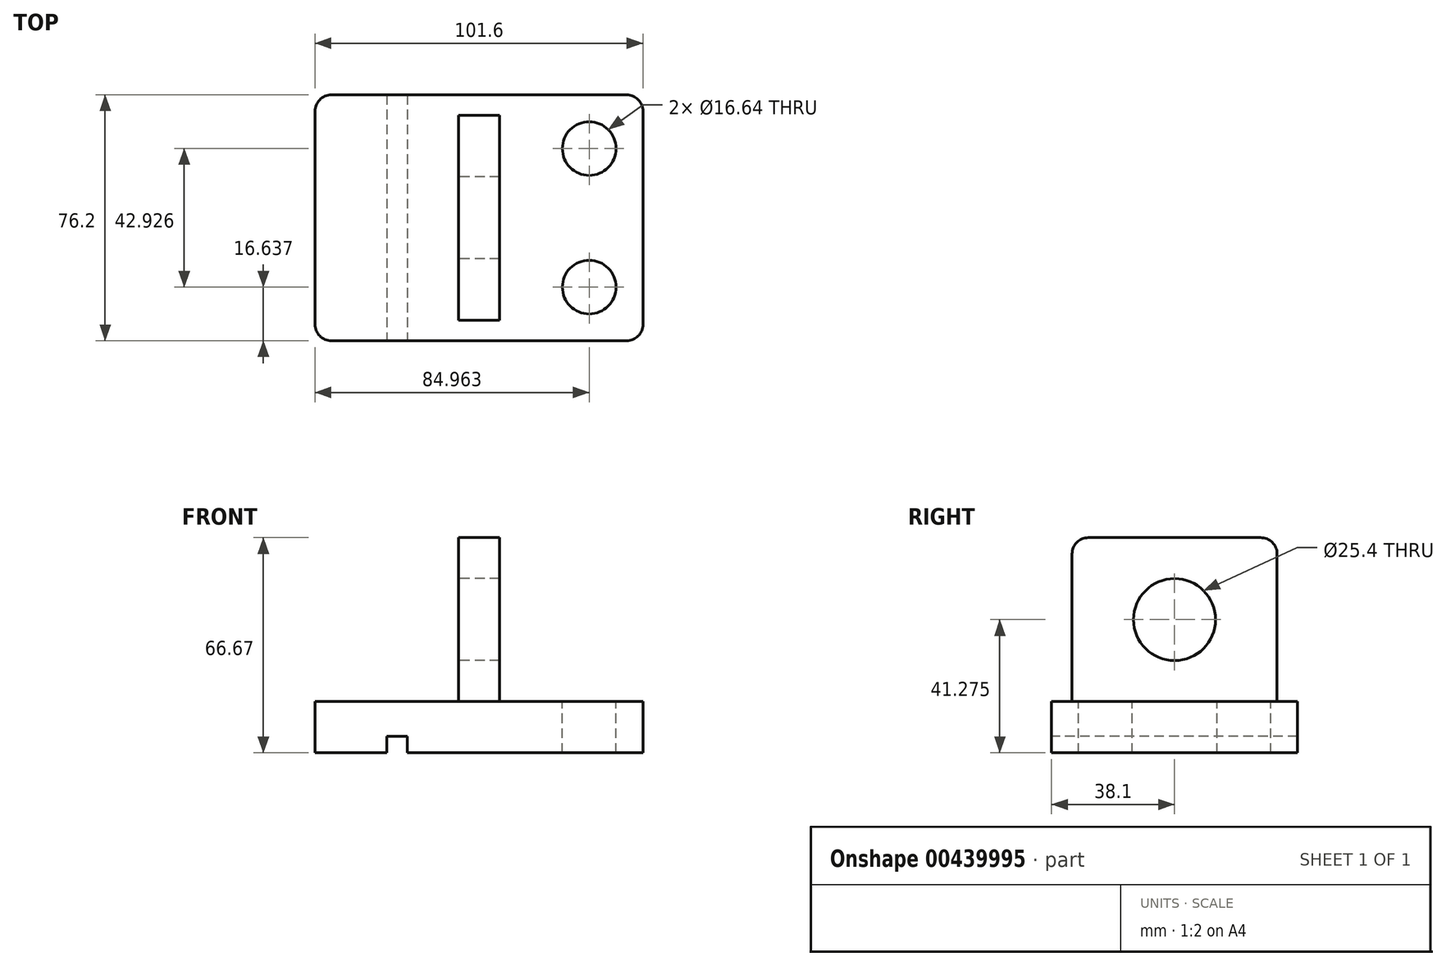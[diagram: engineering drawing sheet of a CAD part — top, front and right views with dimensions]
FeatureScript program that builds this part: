
annotation { "Feature Type Name" : "Feature", "Feature Type Description" : "" }
export const myFeature = defineFeature(function(context is Context, id is Id, definition is map)
    precondition{}
    {
        {
            var Q0;
            Q0=qCreatedBy(makeId("Top.planeOp"),FACE);
            var sketch = newSketch(context, id + "F0", { "sketchPlane" : qUnion([Q0])});
            skLineSegment(sketch, "E0.bottom", {"start": v(50.8, 38.1) * mm, "end": v(-50.8, 38.1) * mm});
            skLineSegment(sketch, "E0.top", {"start": v(50.8, -38.1) * mm, "end": v(-50.8, -38.1) * mm});
            skLineSegment(sketch, "E0.left", {"start": v(50.8, 38.1) * mm, "end": v(50.8, -38.1) * mm});
            skLineSegment(sketch, "E0.right", {"start": v(-50.8, 38.1) * mm, "end": v(-50.8, -38.1) * mm});
            skPoint(sketch, "E0.middle", {"position": v(0, 0) * mm});
            skLineSegment(sketch, "E1.bottom", {"start": v(-6.35, 31.75) * mm, "end": v(6.35, 31.75) * mm});
            skLineSegment(sketch, "E1.top", {"start": v(-6.35, -31.75) * mm, "end": v(6.35, -31.75) * mm});
            skLineSegment(sketch, "E1.left", {"start": v(-6.35, 31.75) * mm, "end": v(-6.35, -31.75) * mm});
            skLineSegment(sketch, "E1.right", {"start": v(6.35, 31.75) * mm, "end": v(6.35, -31.75) * mm});
            skSolve(sketch);
        }
        {
            var Q0;
            Q0 = qSketchRegion(id + "F0", true);
            extrude(context, id + "F1", {"entities" : qUnion([Q0]), "depth" : 15.88 * mm});
        }
        {
            var Q0;
            Q0=makeQuery(id+"F1.opExtrude","SWEPT_EDGE",EDGE,{"disambiguationData":[OSD([sQuery(id+"F0.wireOp",EDGE,"E0.bottom"),sQuery(id+"F0.wireOp",EDGE,"E0.right")])]});
            var Q1;
            Q1=makeQuery(id+"F1.opExtrude","SWEPT_EDGE",EDGE,{"disambiguationData":[OSD([sQuery(id+"F0.wireOp",EDGE,"E0.top"),sQuery(id+"F0.wireOp",EDGE,"E0.right")])]});
            var Q2;
            Q2=makeQuery(id+"F1.opExtrude","SWEPT_EDGE",EDGE,{"disambiguationData":[OSD([sQuery(id+"F0.wireOp",EDGE,"E0.top"),sQuery(id+"F0.wireOp",EDGE,"E0.left")])]});
            var Q3;
            Q3=makeQuery(id+"F1.opExtrude","SWEPT_EDGE",EDGE,{"disambiguationData":[OSD([sQuery(id+"F0.wireOp",EDGE,"E0.bottom"),sQuery(id+"F0.wireOp",EDGE,"E0.left")])]});
            fillet(context, id + "F2", {"entities" : qUnion([Q0, Q1, Q2, Q3]), "radius" : 5.08 * mm, "tangentPropagation" : true, "allowEdgeOverflow" : false});
        }
        {
            var Q0;
            Q0=makeQuery(id+"F1.opExtrude","CAP_FACE",FACE,{"disambiguationData":[OSD([sQuery(id+"F0.wireOp",EDGE,"E0.bottom"),sQuery(id+"F0.wireOp",EDGE,"E0.top"),sQuery(id+"F0.wireOp",EDGE,"E0.left"),sQuery(id+"F0.wireOp",EDGE,"E0.right")])],"isStart":false});
            var sketch = newSketch(context, id + "F3", { "sketchPlane" : qUnion([Q0])});
            skCircle(sketch, "E2", {"center": v(34.16, -21.46) * mm, "radius": 8.32 * mm});
            skCircle(sketch, "E3", {"center": v(34.16, 21.46) * mm, "radius": 8.32 * mm});
            skSolve(sketch);
        }
        {
            var Q0;
            Q0 = qSketchRegion(id + "F3", true);
            extrude(context, id + "F4", {"entities" : qUnion([Q0]), "operationType" : NewBodyOperationType.REMOVE, "oppositeDirection" : true, "depth" : 25.4 * mm});
        }
        {
            var Q0;
            Q0=makeQuery(id+"F0.imprint","IMPRINT",FACE,{"disambiguationData":[TD([[makeQuery(id+"F0.imprint","IMPRINT",EDGE,{"derivedFrom":sQuery(id+"F0.wireOp",EDGE,"E1.bottom")}),-1.0]])]});
            extrude(context, id + "F5", {"entities" : qUnion([Q0]), "operationType" : NewBodyOperationType.ADD, "depth" : 66.67 * mm});
        }
        {
            var Q0;
            Q0=makeQuery(id+"F5.opExtrude","CAP_EDGE",EDGE,{"disambiguationData":[OSD([sQuery(id+"F0.wireOp",EDGE,"E1.top")])],"isStart":false});
            var Q1;
            Q1=makeQuery(id+"F5.opExtrude","CAP_EDGE",EDGE,{"disambiguationData":[OSD([sQuery(id+"F0.wireOp",EDGE,"E1.bottom")])],"isStart":false});
            var Q2;
            Q2=makeQuery(id+"F1.opExtrude","CAP_EDGE",EDGE,{"disambiguationData":[OSD([sQuery(id+"F0.wireOp",EDGE,"E1.bottom")])],"isStart":false});
            var Q3;
            Q3=makeQuery(id+"F1.opExtrude","CAP_EDGE",EDGE,{"disambiguationData":[OSD([sQuery(id+"F0.wireOp",EDGE,"E1.top")])],"isStart":false});
            fillet(context, id + "F6", {"entities" : qUnion([Q0, Q1, Q2, Q3]), "radius" : 5.08 * mm, "tangentPropagation" : true, "allowEdgeOverflow" : false});
        }
        {
            var Q0;
            Q0=makeQuery(id+"F5.opExtrude","SWEPT_FACE",FACE,{"disambiguationData":[OSD([sQuery(id+"F0.wireOp",EDGE,"E1.left")])]});
            var sketch = newSketch(context, id + "F7", { "sketchPlane" : qUnion([Q0])});
            skCircle(sketch, "E4", {"center": v(0, 41.28) * mm, "radius": 12.7 * mm});
            skSolve(sketch);
        }
        {
            var Q0;
            Q0 = qSketchRegion(id + "F7", true);
            extrude(context, id + "F8", {"entities" : qUnion([Q0]), "operationType" : NewBodyOperationType.REMOVE, "oppositeDirection" : true, "depth" : 25.4 * mm});
        }
        {
            var Q0;
            Q0=makeQuery(id+"F1.opExtrude","SWEPT_FACE",FACE,{"disambiguationData":[OSD([sQuery(id+"F0.wireOp",EDGE,"E0.top")])]});
            var sketch = newSketch(context, id + "F9", { "sketchPlane" : qUnion([Q0])});
            skLineSegment(sketch, "E5", {"start": v(-22.23, 0) * mm, "end": v(-22.23, 5.08) * mm});
            skLineSegment(sketch, "E6", {"start": v(-22.23, 5.08) * mm, "end": v(-28.58, 5.08) * mm});
            skLineSegment(sketch, "E7", {"start": v(-28.58, 5.08) * mm, "end": v(-28.58, 0) * mm});
            skLineSegment(sketch, "E8", {"start": v(-28.58, 0) * mm, "end": v(-22.23, 0) * mm});
            skSolve(sketch);
        }
        {
            var Q0;
            Q0 = qSketchRegion(id + "F9", true);
            extrude(context, id + "F10", {"entities" : qUnion([Q0]), "operationType" : NewBodyOperationType.REMOVE, "oppositeDirection" : true, "depth" : 101.6 * mm});
        }
    });
